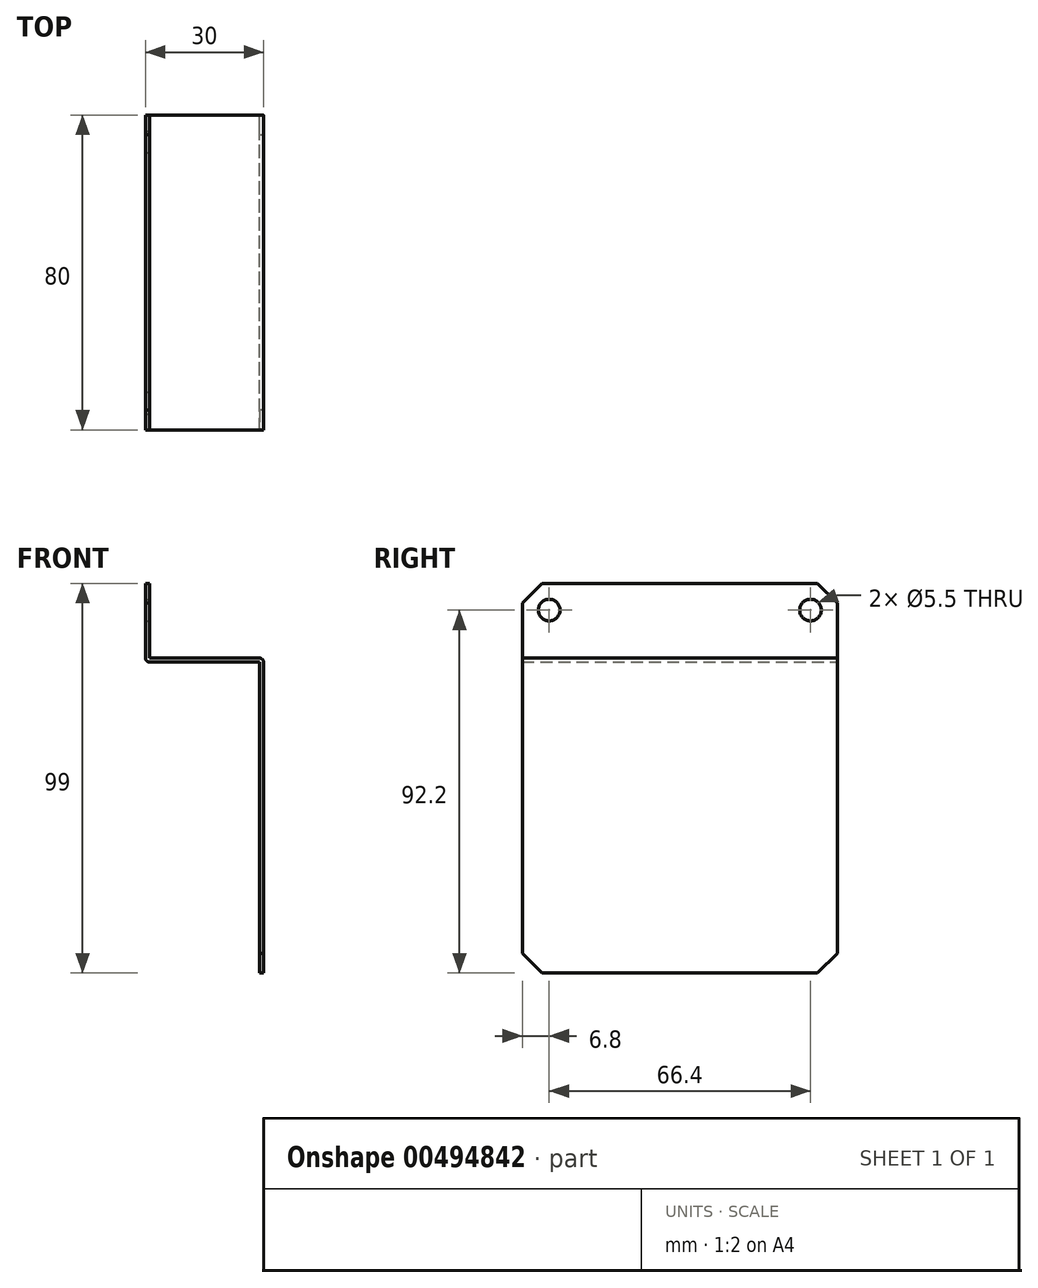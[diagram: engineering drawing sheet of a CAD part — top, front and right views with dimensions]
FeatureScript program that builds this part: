
annotation { "Feature Type Name" : "Feature", "Feature Type Description" : "" }
export const myFeature = defineFeature(function(context is Context, id is Id, definition is map)
    precondition{}
    {
        {
            var Q0;
            Q0=qCreatedBy(makeId("Front.planeOp"),FACE);
            var sketch = newSketch(context, id + "F0", { "sketchPlane" : qUnion([Q0])});
            skLineSegment(sketch, "E0", {"start": v(0, 0) * mm, "end": v(0, 20) * mm});
            skLineSegment(sketch, "E1", {"start": v(0, 20) * mm, "end": v(1, 20) * mm});
            skLineSegment(sketch, "E2", {"start": v(1, 20) * mm, "end": v(1, 1) * mm});
            skLineSegment(sketch, "E3", {"start": v(1, 1) * mm, "end": v(30, 1) * mm});
            skLineSegment(sketch, "E4", {"start": v(30, 1) * mm, "end": v(30, -79) * mm});
            skLineSegment(sketch, "E5", {"start": v(29, -79) * mm, "end": v(30, -79) * mm});
            skLineSegment(sketch, "E6", {"start": v(29, -79) * mm, "end": v(29, 0) * mm});
            skLineSegment(sketch, "E7", {"start": v(29, 0) * mm, "end": v(0, 0) * mm});
            skSolve(sketch);
        }
        {
            var Q0;
            Q0=qSketchRegion(id+"F0",true);
            extrude(context, id + "F1", {"entities" : qUnion([Q0]), "depth" : 80 * mm});
        }
        {
            var Q0;
            Q0=makeQuery(id+"F1.opExtrude","SWEPT_FACE",FACE,{"disambiguationData":[OSD([sQuery(id+"F0.wireOp",EDGE,"E2")])]});
            var sketch = newSketch(context, id + "F2", { "sketchPlane" : qUnion([Q0])});
            skPoint(sketch, "E8", {"position": v(-73.2, 13.2) * mm});
            skPoint(sketch, "E9", {"position": v(-6.8, 13.2) * mm});
            skSolve(sketch);
        }
        {
            var Q0;
            Q0=sQuery(id+"F2.wireOp",VERTEX,"E8");
            var Q1;
            Q1=sQuery(id+"F2.wireOp",VERTEX,"E9");
            var Q2;
            Q2=makeQuery(id+"F1.opExtrude","SWEPT_BODY",BODY,{"disambiguationData":[OSD([sQuery(id+"F0.wireOp",EDGE,"E0"),sQuery(id+"F0.wireOp",EDGE,"E1"),sQuery(id+"F0.wireOp",EDGE,"E2"),sQuery(id+"F0.wireOp",EDGE,"E3"),sQuery(id+"F0.wireOp",EDGE,"E4"),sQuery(id+"F0.wireOp",EDGE,"E5"),sQuery(id+"F0.wireOp",EDGE,"E6"),sQuery(id+"F0.wireOp",EDGE,"E7")])]});
            hole(context, id + "F3", {"style" : HoleStyle.SIMPLE, "endStyle" : HoleEndStyle.THROUGH, "standardTappedOrClearance" : lookupTablePath({ "standard" : "ISO", "fit" : "Normal", "size" : "M5", "type" : "Clearance" }), "standardBlindInLast" : lookupTablePath({ "fit" : "Standard", "standard" : "ISO", "size" : "M5", "type" : "Clearance" }), "holeDiameter" : 5.5 * mm, "isTappedThrough" : true, "tappedDepth" : 7.6 * mm, "tapClearance" : 3, "locations" : qUnion([Q0, Q1]), "scope" : qUnion([Q2])});
        }
        {
            var Q0;
            Q0=makeQuery(id+"F1.opExtrude","CAP_EDGE",EDGE,{"disambiguationData":[OSD([sQuery(id+"F0.wireOp",EDGE,"E1")])],"isStart":false});
            var Q1;
            Q1=makeQuery(id+"F1.opExtrude","CAP_EDGE",EDGE,{"disambiguationData":[OSD([sQuery(id+"F0.wireOp",EDGE,"E1")])],"isStart":true});
            var Q2;
            Q2=makeQuery(id+"F1.opExtrude","CAP_EDGE",EDGE,{"disambiguationData":[OSD([sQuery(id+"F0.wireOp",EDGE,"E5")])],"isStart":true});
            var Q3;
            Q3=makeQuery(id+"F1.opExtrude","CAP_EDGE",EDGE,{"disambiguationData":[OSD([sQuery(id+"F0.wireOp",EDGE,"E5")])],"isStart":false});
            chamfer(context, id + "F4", {"entities" : qUnion([Q0, Q1, Q2, Q3]), "width" : 5 * mm, "tangentPropagation" : true});
        }
        {
            var Q0;
            Q0=makeQuery(id+"F1.opExtrude","SWEPT_EDGE",EDGE,{"disambiguationData":[OSD([sQuery(id+"F0.wireOp",EDGE,"E3"),sQuery(id+"F0.wireOp",EDGE,"E4")])]});
            var Q1;
            Q1=makeQuery(id+"F1.opExtrude","SWEPT_EDGE",EDGE,{"disambiguationData":[OSD([sQuery(id+"F0.wireOp",EDGE,"E0"),sQuery(id+"F0.wireOp",EDGE,"E7")])]});
            fillet(context, id + "F5", {"entities" : qUnion([Q0, Q1]), "radius" : 1 * mm, "tangentPropagation" : true, "allowEdgeOverflow" : false});
        }
    });
